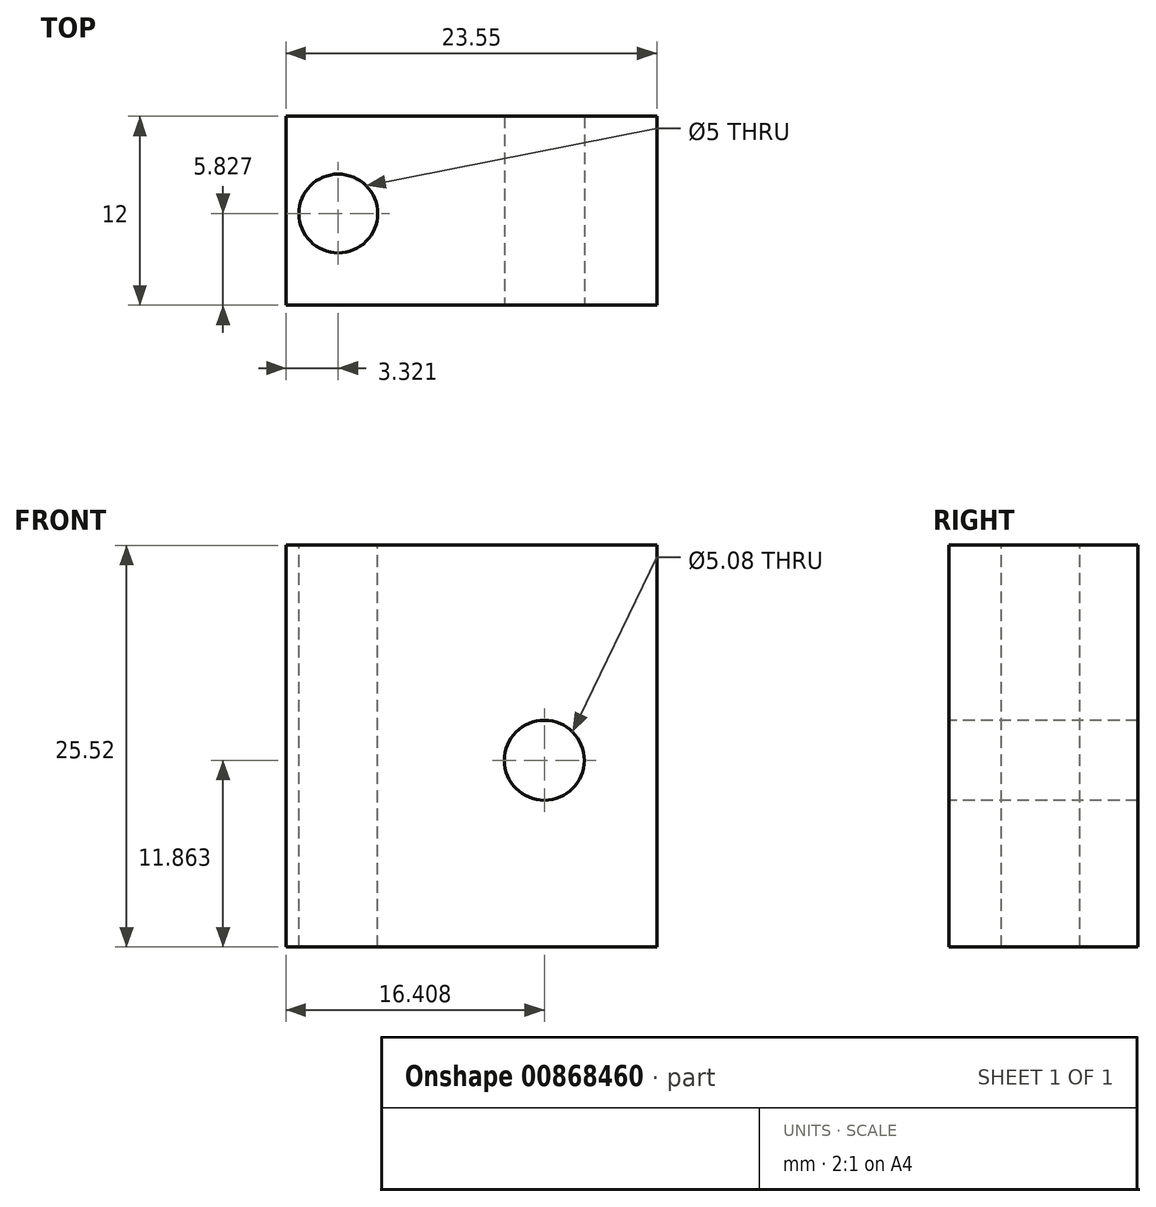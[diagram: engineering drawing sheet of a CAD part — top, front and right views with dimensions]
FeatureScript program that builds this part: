
annotation { "Feature Type Name" : "Feature", "Feature Type Description" : "" }
export const myFeature = defineFeature(function(context is Context, id is Id, definition is map)
    precondition{}
    {
        {
            var Q0;
            Q0=qCreatedBy(makeId("Front.planeOp"),FACE);
            var sketch = newSketch(context, id + "F0", { "sketchPlane" : qUnion([Q0])});
            skLineSegment(sketch, "E0.bottom", {"start": v(-4.6, 0) * mm, "end": v(-28.15, 0) * mm});
            skLineSegment(sketch, "E0.top", {"start": v(-4.6, 25.52) * mm, "end": v(-28.15, 25.52) * mm});
            skLineSegment(sketch, "E0.left", {"start": v(-4.6, 0) * mm, "end": v(-4.6, 25.52) * mm});
            skLineSegment(sketch, "E0.right", {"start": v(-28.15, 0) * mm, "end": v(-28.15, 25.52) * mm});
            skSolve(sketch);
        }
        {
            var Q0;
            Q0=makeQuery(id+"F0.imprint","IMPRINT",FACE,{"disambiguationData":[TD([[makeQuery(id+"F0.imprint","IMPRINT",EDGE,{"derivedFrom":sQuery(id+"F0.wireOp",EDGE,"E0.bottom")}),-1.0]])]});
            extrude(context, id + "F1", {"entities" : qUnion([Q0]), "depth" : 12 * mm, "offsetDistance" : 25.4 * mm});
        }
        {
            var Q0;
            Q0=makeQuery(id+"F1.opExtrude","SWEPT_FACE",FACE,{"disambiguationData":[OSD([sQuery(id+"F0.wireOp",EDGE,"E0.top")])]});
            var sketch = newSketch(context, id + "F2", { "sketchPlane" : qUnion([Q0])});
            skCircle(sketch, "E1", {"center": v(-24.83, -6.17) * mm, "radius": 5.23 * mm});
            skSolve(sketch);
        }
        {
            var Q0;
            Q0=sQuery(id+"F2.wireOp",VERTEX,"E1.center");
            var Q1;
            Q1=makeQuery(id+"F1.opExtrude","SWEPT_BODY",BODY,{"disambiguationData":[OSD([sQuery(id+"F0.wireOp",EDGE,"E0.bottom"),sQuery(id+"F0.wireOp",EDGE,"E0.top"),sQuery(id+"F0.wireOp",EDGE,"E0.left"),sQuery(id+"F0.wireOp",EDGE,"E0.right")])]});
            hole(context, id + "F3", {"style" : HoleStyle.SIMPLE, "endStyle" : HoleEndStyle.THROUGH, "holeDiameter" : 5 * mm, "majorDiameter" : 6.35 * mm, "isTappedThrough" : true, "tappedDepth" : 12.7 * mm, "tapClearance" : 3, "locations" : qUnion([Q0]), "scope" : qUnion([Q1])});
        }
        {
            var Q0;
            Q0=makeQuery(id+"F1.opExtrude","CAP_FACE",FACE,{"disambiguationData":[OSD([sQuery(id+"F0.wireOp",EDGE,"E0.bottom"),sQuery(id+"F0.wireOp",EDGE,"E0.top"),sQuery(id+"F0.wireOp",EDGE,"E0.left"),sQuery(id+"F0.wireOp",EDGE,"E0.right")])],"isStart":false});
            var sketch = newSketch(context, id + "F4", { "sketchPlane" : qUnion([Q0])});
            skSolve(sketch);
        }
        {
            var Q0;
            Q0=makeQuery(id+"F4.imprint","IMPRINT",FACE,{"disambiguationData":[TD([[makeQuery(id+"F4.imprint","IMPRINT",EDGE,{"derivedFrom":makeQuery(id+"F1.opExtrude","CAP_EDGE",EDGE,{"disambiguationData":[OSD([sQuery(id+"F0.wireOp",EDGE,"E0.bottom")])],"isStart":false})}),-1.0]])]});
            var sketch = newSketch(context, id + "F5", { "sketchPlane" : qUnion([Q0])});
            skCircle(sketch, "E2", {"center": v(-11.74, 11.86) * mm, "radius": 4.83 * mm});
            skSolve(sketch);
        }
        {
            var Q0;
            Q0=sQuery(id+"F5.wireOp",VERTEX,"E2.center");
            var Q1;
            Q1=makeQuery(id+"F1.opExtrude","SWEPT_BODY",BODY,{"disambiguationData":[OSD([sQuery(id+"F0.wireOp",EDGE,"E0.bottom"),sQuery(id+"F0.wireOp",EDGE,"E0.top"),sQuery(id+"F0.wireOp",EDGE,"E0.left"),sQuery(id+"F0.wireOp",EDGE,"E0.right")])]});
            hole(context, id + "F6", {"style" : HoleStyle.SIMPLE, "endStyle" : HoleEndStyle.THROUGH, "holeDiameter" : 5.08 * mm, "majorDiameter" : 6.35 * mm, "isTappedThrough" : true, "tappedDepth" : 12.7 * mm, "tapClearance" : 3, "locations" : qUnion([Q0]), "scope" : qUnion([Q1])});
        }
    });
